# Revit family: Domotics-DomesticRanges-GEWISS-SYSTEM_POWER-SOCKET-OUTLET_USA_125V
name_source: partatom
category: Apparecchi elettrici
revit_build: Autodesk Revit 2016 (Build: 20161004_0715(x64)
units: mm (PartAtom-declared; Revit-internal decimal feet)

## family parameters
Condiviso = Sì
Host = Superficie
Mantenere orientamento annotazione = Sì
Punto di calcolo locali = Sì
Quota connettore circolare = Usa diametro
Taglio con vuoti quando caricato = Sì
Tipo di parte = Normale

## types (2) — shared parameters
Carico apparente = 0 VA
Catalogue = DOMOTICS
Catalogue Range = SYSTEM - DOMESTIC RANGE
Description. = USA
Electrocod = 0131
For plug pins = Flat
IDF = 6c3631f0-4860-44a4-90e4-88446daf7761
IDT = fad1e021-e11a-42c0-b11a-ea34ad6a3e0e
Immagine tipo = GW21214.jpg
N. poli = 1
No. SYSTEM modules = 1
Produttore = GEWISS S.p.A.
Prospetto di default = 1219 mm
SEO = Socket outlet
Shape = Parallel horizontal
Standard = USA
Standard: = USA
TXT ELETTRICO = 15
Technical sheet = https://www.gewiss.com
Tipo = System Prese Usa_GENERICO : GW21214 Presa 2P+T 15A 125V standard USA nero
URL = https://www.gewiss.com
Version file RFA = 19.4
Volt = 230 V
Voltage = 250/125V AC
Voltage: = 250/125V AC

## per-type parameters (varying)
| type | Colour | Description: | Descrizione | EAN code | Modello |
| GW20214 - 2P+E 15A 125V usa s.-outlet white | White | 2P+E - 15A - 125V ac | 2P+E 15A 125V USA S.-OUTLET SY/WT | 8011564000674 | GW20214 |
| GW21214 - 2P+E 15A 125V usa s.-outlet black | Black | 2P+E - 15A 125V ac | 2P+E 15A 125V USA S.-OUTLET SY/BK | 8011564128545 | GW21214 |

## geometry (parser evidence)
native form markers: Sweep x2
no freeform markers — native parametric forms only
